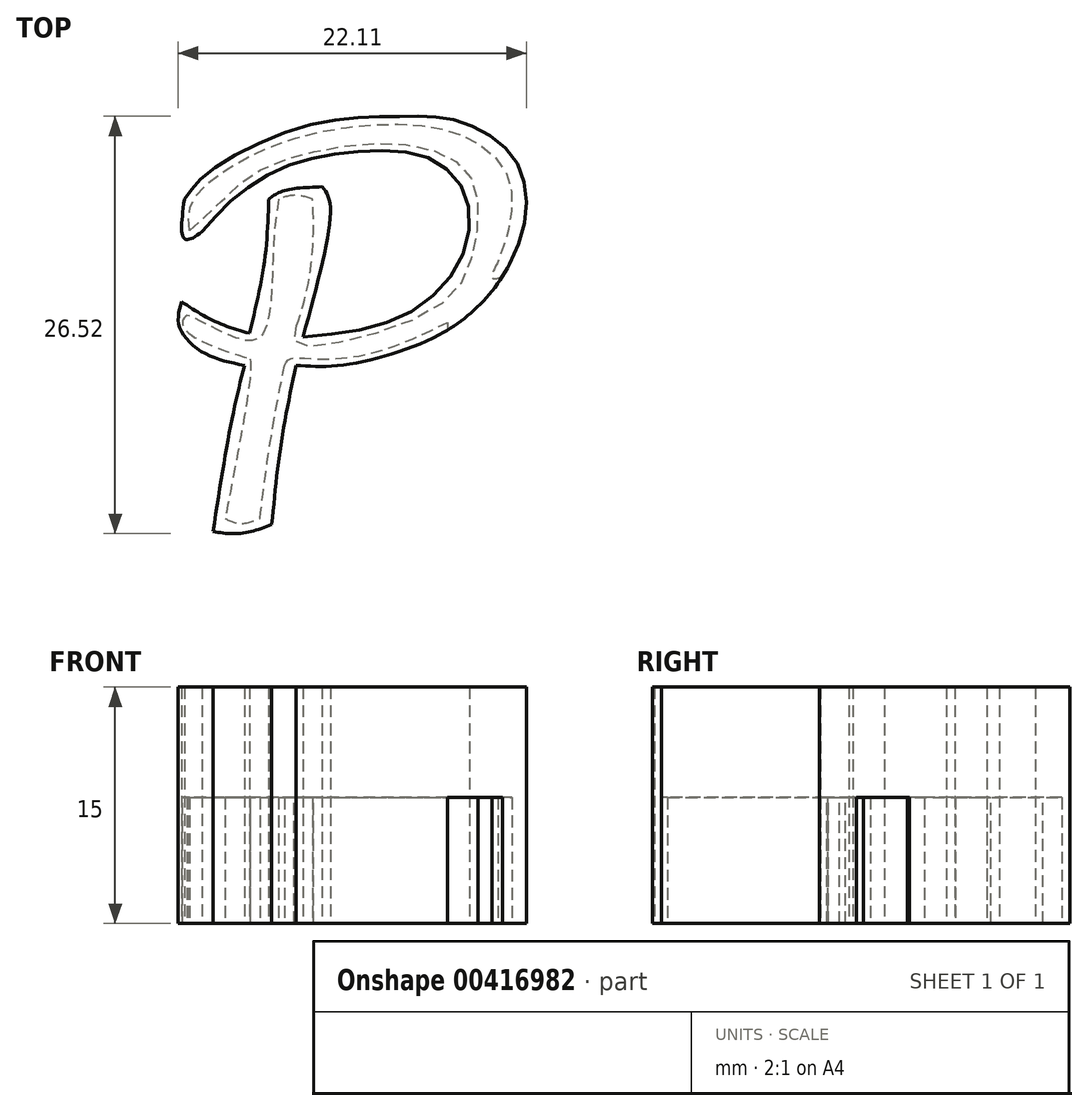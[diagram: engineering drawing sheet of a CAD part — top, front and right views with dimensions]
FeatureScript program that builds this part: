
annotation { "Feature Type Name" : "Feature", "Feature Type Description" : "" }
export const myFeature = defineFeature(function(context is Context, id is Id, definition is map)
    precondition{}
    {
        {
            var Q0;
            Q0=qCreatedBy(makeId("Top.planeOp"),FACE);
            var sketch = newSketch(context, id + "F0", { "sketchPlane" : qUnion([Q0])});
            skFitSpline(sketch, "E0", {"points": [v(-29.52, 16.09) * mm, v(-21.73, 24.17) * mm, v(-15.95, 22) * mm], "startDerivative": vector(5.63, 25.07) * mm, "endDerivative": vector(12.64, -16.05) * mm});
            skFitSpline(sketch, "E1", {"points": [v(-29.52, 16.09) * mm, v(-29.52, 11.79) * mm, v(-26.49, 8.08) * mm, v(-18.6, 8.9) * mm, v(-11.86, 14.14) * mm], "startDerivative": vector(-2.65, -20.74) * mm, "endDerivative": vector(20.85, 20.56) * mm});
            skFitSpline(sketch, "E2", {"points": [v(-15.95, 22) * mm, v(-15.95, 19.53) * mm, v(-19.6, 15.68) * mm, v(-26.31, 14.5) * mm], "startDerivative": vector(1.91, -9.63) * mm, "endDerivative": vector(-17.6, -0.63) * mm});
            skFitSpline(sketch, "E3", {"points": [v(-26.31, 14.5) * mm, v(-26.31, 12.31) * mm, v(-24.25, 10.14) * mm, v(-18.22, 11.13) * mm, v(-11.16, 17.2) * mm], "startDerivative": vector(-1.95, -12.78) * mm, "endDerivative": vector(19.15, 20.18) * mm});
            skFitSpline(sketch, "E4", {"points": [v(-11.16, 17.2) * mm, v(-8.94, 21.18) * mm, v(-5, 24.17) * mm, v(-0.8, 24.22) * mm, v(2.15, 22.9) * mm], "startDerivative": vector(7.17, 15.76) * mm, "endDerivative": vector(12.55, -6.92) * mm});
            skFitSpline(sketch, "E5", {"points": [v(2.15, 22.9) * mm, v(2.96, 23.95) * mm, v(5.9, 24.4) * mm], "startDerivative": vector(1.46, 2.97) * mm, "endDerivative": vector(5.76, 0.2) * mm});
            skFitSpline(sketch, "E6", {"points": [v(-11.86, 14.14) * mm, v(-11.86, 10.9) * mm, v(-9.94, 8.05) * mm, v(-6.14, 8.37) * mm], "startDerivative": vector(-1.2, -9.86) * mm, "endDerivative": vector(11.9, 3.41) * mm});
            skFitSpline(sketch, "E7", {"points": [v(-6.14, 8.37) * mm, v(-2.1, 12.17) * mm, v(0.93, 17.2) * mm], "startDerivative": vector(8.72, 7.18) * mm, "endDerivative": vector(5.42, 10.46) * mm});
            skFitSpline(sketch, "E8", {"points": [v(0.93, 17.2) * mm, v(0.93, 11.63) * mm, v(3.05, 8.96) * mm, v(6.72, 9.41) * mm, v(12.48, 14.14) * mm], "startDerivative": vector(-2.53, -22.33) * mm, "endDerivative": vector(18.4, 18.48) * mm});
            skFitSpline(sketch, "E9", {"points": [v(5.9, 24.4) * mm, v(4.28, 19.57) * mm, v(4.12, 12.84) * mm, v(5.03, 11.7) * mm, v(7.94, 12.57) * mm, v(12.9, 17.2) * mm], "startDerivative": vector(-8.65, -19.72) * mm, "endDerivative": vector(19.75, 21.62) * mm});
            skFitSpline(sketch, "E10", {"points": [v(12.9, 17.2) * mm, v(14.78, 20.91) * mm, v(18.92, 23.71) * mm, v(21.5, 24.4) * mm, v(24.04, 24.4) * mm, v(25.8, 23.42) * mm, v(26.53, 22.62) * mm, v(26.53, 21.34) * mm], "startDerivative": vector(7.3, 21.14) * mm, "endDerivative": vector(-1.85, -13.72) * mm});
            skFitSpline(sketch, "E11", {"points": [v(26.53, 21.34) * mm, v(25.28, 20.25) * mm, v(23.65, 19.61) * mm], "startDerivative": vector(-2.36, -2.44) * mm, "endDerivative": vector(-3.4, -1.02) * mm});
            skFitSpline(sketch, "E12", {"points": [v(23.65, 19.61) * mm, v(23.65, 21.34) * mm, v(22.59, 22.59) * mm, v(19.84, 22.59) * mm, v(16.5, 19.47) * mm, v(15.44, 17.2) * mm, v(15.32, 13.21) * mm, v(17.37, 9.82) * mm, v(20.92, 9.28) * mm, v(26.53, 12.94) * mm, v(29.59, 16.3) * mm], "startDerivative": vector(3.16, 25.43) * mm, "endDerivative": vector(23.14, 28.11) * mm});
            skFitSpline(sketch, "E13", {"points": [v(12.48, 14.14) * mm, v(12.48, 11.74) * mm, v(14.3, 8.6) * mm, v(16.78, 7.12) * mm, v(20.7, 7.08) * mm, v(24.82, 9.2) * mm, v(29.53, 13.7) * mm], "startDerivative": vector(-2.82, -18.44) * mm, "endDerivative": vector(21.23, 22.93) * mm});
            skFitSpline(sketch, "E14", {"points": [v(29.59, 16.3) * mm, v(30.44, 19.1) * mm, v(33.77, 22.87) * mm, v(38.3, 24.54) * mm, v(41.2, 24.05) * mm, v(42.85, 22.55) * mm, v(43.33, 20.19) * mm, v(41.47, 17.24) * mm, v(36.7, 14.68) * mm, v(32.8, 14.36) * mm], "startDerivative": vector(5.2, 27.04) * mm, "endDerivative": vector(-32.45, 0.66) * mm});
            skFitSpline(sketch, "E15", {"points": [v(32.8, 14.36) * mm, v(32.8, 12.43) * mm, v(34.32, 10.34) * mm, v(38.4, 10.26) * mm, v(45.36, 14.68) * mm, v(50.16, 20.77) * mm], "startDerivative": vector(-1.91, -14.46) * mm, "endDerivative": vector(16.23, 24.12) * mm});
            skFitSpline(sketch, "E16", {"points": [v(29.53, 13.7) * mm, v(29.53, 12.01) * mm, v(31.32, 8.9) * mm, v(35.92, 7.67) * mm, v(42.01, 9.84) * mm, v(46.54, 13.35) * mm, v(49.86, 17.2) * mm, v(51.72, 20.2) * mm], "startDerivative": vector(-2.56, -18.37) * mm, "endDerivative": vector(12.98, 22.51) * mm});
            skLineSegment(sketch, "E17", {"start": v(50.16, 20.77) * mm, "end": v(51.72, 20.2) * mm});
            skFitSpline(sketch, "E18", {"points": [v(-26.18, 16.08) * mm, v(-25.34, 19.37) * mm, v(-22.06, 22.5) * mm, v(-19.63, 22.7) * mm, v(-18.72, 21.74) * mm, v(-18.99, 19.53) * mm, v(-20.98, 17.43) * mm, v(-24.32, 16.09) * mm, v(-26.18, 16.08) * mm]});
            skFitSpline(sketch, "E19", {"points": [v(-8.92, 15.05) * mm, v(-8.16, 18.38) * mm, v(-5.66, 21.9) * mm, v(-2.78, 22.4) * mm, v(1.45, 20.49) * mm], "startDerivative": vector(1.92, 13.6) * mm, "endDerivative": vector(15.76, -8.92) * mm});
            skFitSpline(sketch, "E20", {"points": [v(-8.92, 15.05) * mm, v(-8.92, 12.3) * mm, v(-7.52, 10.82) * mm, v(-5.4, 11.59) * mm, v(-1.43, 16.26) * mm, v(1.45, 20.49) * mm], "startDerivative": vector(-2.38, -16.28) * mm, "endDerivative": vector(10.96, 16.58) * mm});
            skFitSpline(sketch, "E21", {"points": [v(32.96, 15.95) * mm, v(33.77, 19.4) * mm, v(37.64, 22.68) * mm, v(40.06, 22.25) * mm, v(40.28, 19.67) * mm, v(36.73, 16.81) * mm, v(32.96, 15.95) * mm]});
            skLineSegment(sketch, "E22", {"start": v(-26.49, 8.08) * mm, "end": v(-26.49, 0) * mm});
            skFitSpline(sketch, "E23", {"points": [v(-39.17, 6.72) * mm, v(-38.6, 11.78) * mm, v(-37.63, 16.84) * mm], "startDerivative": vector(0.97, 10.16) * mm, "endDerivative": vector(2.1, 10.07) * mm});
            skFitSpline(sketch, "E24", {"points": [v(-37.63, 16.84) * mm, v(-34.88, 16.84) * mm, v(-29.82, 18.18) * mm, v(-25.73, 20.94) * mm, v(-23.16, 25.68) * mm, v(-23.8, 30.03) * mm, v(-27.45, 32.4) * mm, v(-31.17, 32.65) * mm, v(-36.87, 32.08) * mm, v(-43.4, 28.94) * mm, v(-44.72, 27.4) * mm], "startDerivative": vector(32.12, -2.24) * mm, "endDerivative": vector(-16.47, -20.53) * mm});
            skFitSpline(sketch, "E25", {"points": [v(-44.72, 27.4) * mm, v(-44.72, 24.9) * mm, v(-43.59, 25.35) * mm], "startDerivative": vector(-0.9, -6.83) * mm, "endDerivative": vector(3.83, 3.23) * mm});
            skFitSpline(sketch, "E26", {"points": [v(-43.59, 25.35) * mm, v(-41.22, 27.74) * mm, v(-37.57, 29.72) * mm, v(-33.41, 30.43) * mm, v(-29.25, 30.04) * mm, v(-26.82, 27.48) * mm, v(-27.33, 23.26) * mm, v(-31.24, 19.8) * mm, v(-37.2, 18.65) * mm], "startDerivative": vector(19.6, 22.42) * mm, "endDerivative": vector(-42.14, -3.8) * mm});
            skFitSpline(sketch, "E27", {"points": [v(-37.2, 18.65) * mm, v(-35.46, 27.03) * mm, v(-35.97, 28.19) * mm], "startDerivative": vector(3.92, 14.3) * mm, "endDerivative": vector(-2.43, 3.12) * mm});
            skFitSpline(sketch, "E28", {"points": [v(-35.97, 28.19) * mm, v(-38.52, 27.9) * mm, v(-39.36, 27.39) * mm], "startDerivative": vector(-4.73, -0.2) * mm, "endDerivative": vector(-1.82, -1.5) * mm});
            skFitSpline(sketch, "E29", {"points": [v(-39.17, 6.72) * mm, v(-41.13, 6.17) * mm, v(-42.9, 6.28) * mm], "startDerivative": vector(-3.82, -1.4) * mm, "endDerivative": vector(-3.65, 0.53) * mm});
            skFitSpline(sketch, "E30", {"points": [v(-42.9, 6.28) * mm, v(-41.77, 13.06) * mm, v(-40.91, 16.84) * mm], "startDerivative": vector(1.97, 12.75) * mm, "endDerivative": vector(2.02, 8.15) * mm});
            skFitSpline(sketch, "E31", {"points": [v(-40.91, 16.84) * mm, v(-43.59, 17.7) * mm, v(-45.06, 19.36) * mm, v(-44.9, 20.89) * mm], "startDerivative": vector(-7.42, 1.53) * mm, "endDerivative": vector(1.61, 5.39) * mm});
            skFitSpline(sketch, "E32", {"points": [v(-44.9, 20.89) * mm, v(-42.9, 19.69) * mm, v(-40.59, 18.88) * mm], "startDerivative": vector(3.9, -2.64) * mm, "endDerivative": vector(4.7, -1.38) * mm});
            skFitSpline(sketch, "E33", {"points": [v(-40.59, 18.88) * mm, v(-39.64, 23.42) * mm, v(-39.36, 27.39) * mm], "startDerivative": vector(2.16, 8.87) * mm, "endDerivative": vector(0.27, 8.13) * mm});
            skSolve(sketch);
        }
        {
            var Q0;
            {var subQ1=sQuery(id+"F0.wireOp",EDGE,"E23");Q0=makeQuery(id+"F0.imprint","IMPRINT",FACE,{"disambiguationData":[TD([[makeQuery(id+"F0.imprint","IMPRINT",EDGE,{"derivedFrom":subQ1}),1.0]])]});}
            var Q1;
            {var subQ3=sQuery(id+"F0.wireOp",EDGE,"E0");Q1=makeQuery(id+"F0.imprint","IMPRINT",FACE,{"disambiguationData":[TD([[makeQuery(id+"F0.imprint","IMPRINT",EDGE,{"derivedFrom":subQ3}),-1.0]])]});}
            extrude(context, id + "F1", {"entities" : qUnion([Q0, Q1]), "depth" : 15 * mm});
        }
        {
            var Q0;
            {var subQ0=sQuery(id+"F0.wireOp",EDGE,"E0");var subQ2=sQuery(id+"F0.wireOp",EDGE,"E33");var subQ6=sQuery(id+"F0.wireOp",EDGE,"E32");var subQ8=sQuery(id+"F0.wireOp",EDGE,"E31");var subQ9=sQuery(id+"F0.wireOp",EDGE,"E30");var subQ12=sQuery(id+"F0.wireOp",EDGE,"E29");var subQ13=sQuery(id+"F0.wireOp",EDGE,"E28");var subQ14=sQuery(id+"F0.wireOp",EDGE,"E27");var subQ15=sQuery(id+"F0.wireOp",EDGE,"E26");var subQ16=sQuery(id+"F0.wireOp",EDGE,"E25");var subQ17=sQuery(id+"F0.wireOp",EDGE,"E24");var subQ18=sQuery(id+"F0.wireOp",EDGE,"E0");var subQ19=sQuery(id+"F0.wireOp",EDGE,"E23");var subQ20=sQuery(id+"F0.wireOp",EDGE,"E8");var subQ21=sQuery(id+"F0.wireOp",EDGE,"E7");var subQ22=sQuery(id+"F0.wireOp",EDGE,"E6");var subQ23=sQuery(id+"F0.wireOp",EDGE,"E5");var subQ24=sQuery(id+"F0.wireOp",EDGE,"E4");var subQ25=sQuery(id+"F0.wireOp",EDGE,"E9");var subQ26=sQuery(id+"F0.wireOp",EDGE,"E21");var subQ27=sQuery(id+"F0.wireOp",EDGE,"E3");var subQ28=sQuery(id+"F0.wireOp",EDGE,"E1");var subQ29=sQuery(id+"F0.wireOp",EDGE,"E2");var subQ30=sQuery(id+"F0.wireOp",EDGE,"E10");var subQ31=sQuery(id+"F0.wireOp",EDGE,"E11");var subQ32=sQuery(id+"F0.wireOp",EDGE,"E12");var subQ33=sQuery(id+"F0.wireOp",EDGE,"E13");var subQ34=sQuery(id+"F0.wireOp",EDGE,"E14");var subQ35=sQuery(id+"F0.wireOp",EDGE,"E15");var subQ36=sQuery(id+"F0.wireOp",EDGE,"E16");var subQ37=sQuery(id+"F0.wireOp",EDGE,"E17");var subQ38=sQuery(id+"F0.wireOp",EDGE,"E19");var subQ39=sQuery(id+"F0.wireOp",EDGE,"E20");Q0=makeQuery(id+"FnfwpsjC2COg8uT_1.boolean.opBoolean","SPLIT",FACE,{"disambiguationData":[TD([makeQuery(id+"F1.opExtrude","SWEPT_FACE",FACE,{"disambiguationData":[OSD([subQ18])]})])],"derivedFrom":makeQuery(id+"F1.opExtrude","CAP_FACE",FACE,{"disambiguationData":[OSD([subQ18,subQ28,subQ29,subQ27,subQ24,subQ23,subQ22,subQ21,subQ20,subQ25,subQ30,subQ31,subQ32,subQ33,subQ34,subQ35,subQ36,subQ37,sQuery(id+"F0.wireOp",EDGE,"E18"),subQ38,subQ39,subQ26,subQ19,subQ17,subQ16,subQ15,subQ14,subQ13,subQ12,subQ9,subQ8,subQ6,subQ2,subQ0])],"isStart":true})});}
            var sketch = newSketch(context, id + "F2", { "sketchPlane" : qUnion([Q0])});
            skFitSpline(sketch, "E34", {"points": [v(-7.05, -22.42) * mm, v(-4.76, -23.59) * mm, v(-1.87, -23.71) * mm, v(2.2, -22.24) * mm], "startDerivative": vector(7.38, -4.6) * mm, "endDerivative": vector(10.81, 4.77) * mm});
            skFitSpline(sketch, "E35", {"points": [v(2.2, -22.24) * mm, v(3.4, -23.59) * mm, v(4.89, -23.59) * mm, v(4.9, -23.59) * mm], "startDerivative": vector(1.78, -3.5) * mm, "endDerivative": vector(0.19, -0.04) * mm});
            skFitSpline(sketch, "E36", {"points": [v(4.9, -23.59) * mm, v(3.69, -19.61) * mm, v(3.13, -14.5) * mm, v(3.88, -11) * mm, v(7.5, -11.57) * mm, v(12.9, -16.09) * mm], "startDerivative": vector(-7.2, 20.2) * mm, "endDerivative": vector(21.14, -21.2) * mm});
            skFitSpline(sketch, "E37", {"points": [v(-6.01, -9.18) * mm, v(-3.7, -11.12) * mm, v(-1.23, -14.14) * mm, v(0.87, -18.02) * mm], "startDerivative": vector(7.8, -6) * mm, "endDerivative": vector(5.45, -11.06) * mm});
            skFitSpline(sketch, "E38", {"points": [v(0.87, -18.02) * mm, v(1.57, -18.02) * mm, v(1.16, -14.78) * mm, v(2.12, -10.74) * mm, v(4.69, -9.55) * mm, v(8, -10.74) * mm, v(13.04, -15.04) * mm], "startDerivative": vector(11.28, -3.14) * mm, "endDerivative": vector(21.76, -20.55) * mm});
            skFitSpline(sketch, "E39", {"points": [v(16.32, -9.88) * mm, v(18.15, -8.49) * mm, v(21.8, -8.93) * mm, v(29.59, -15.35) * mm], "startDerivative": vector(7.05, 7.31) * mm, "endDerivative": vector(16.95, -16.56) * mm});
            skFitSpline(sketch, "E40", {"points": [v(13.04, -15.04) * mm, v(13.04, -12.56) * mm, v(14.6, -9.02) * mm, v(17.92, -7.33) * mm, v(22.52, -8.37) * mm, v(29.53, -14.14) * mm], "startDerivative": vector(-1.45, 15.7) * mm, "endDerivative": vector(25.27, -24.15) * mm});
            skFitSpline(sketch, "E41", {"points": [v(12.9, -16.09) * mm, v(14.9, -20.41) * mm, v(19.74, -23.72) * mm, v(24.12, -23.98) * mm, v(25.9, -21.89) * mm], "startDerivative": vector(5.56, -17.35) * mm, "endDerivative": vector(7.1, 12.74) * mm});
            skFitSpline(sketch, "E42", {"points": [v(29.59, -15.35) * mm, v(31.16, -19.52) * mm, v(35.37, -23.38) * mm, v(39.89, -24.04) * mm, v(41.96, -22.95) * mm], "startDerivative": vector(4.34, -16.27) * mm, "endDerivative": vector(9.61, 7.15) * mm});
            skFitSpline(sketch, "E43", {"points": [v(41.96, -22.95) * mm, v(42.83, -20.46) * mm, v(40.82, -17.49) * mm, v(36.23, -15.16) * mm, v(32.5, -14.85) * mm], "startDerivative": vector(6.75, 11.6) * mm, "endDerivative": vector(-14.39, -0.1) * mm});
            skFitSpline(sketch, "E44", {"points": [v(32.5, -14.85) * mm, v(32.08, -12.6) * mm, v(33.51, -9.88) * mm, v(37.87, -9.35) * mm, v(43.64, -12.54) * mm, v(48.24, -17.3) * mm, v(50.27, -20.1) * mm], "startDerivative": vector(-5.9, 17.41) * mm, "endDerivative": vector(11.9, -17.42) * mm});
            skFitSpline(sketch, "E45", {"points": [v(29.53, -14.14) * mm, v(30.02, -14.14) * mm, v(30.05, -13.7) * mm], "startDerivative": vector(1.2, -0.23) * mm, "endDerivative": vector(-0.16, 1.13) * mm});
            skFitSpline(sketch, "E46", {"points": [v(30.05, -13.7) * mm, v(30.05, -12.45) * mm, v(30.92, -10.3) * mm, v(32.8, -8.62) * mm, v(37.33, -8.23) * mm, v(44.03, -11.82) * mm, v(50.87, -19.69) * mm], "startDerivative": vector(-1.32, 12.84) * mm, "endDerivative": vector(24.94, -32.81) * mm});
            skFitSpline(sketch, "E47", {"points": [v(50.87, -19.69) * mm, v(50.72, -20.07) * mm, v(50.27, -20.1) * mm], "startDerivative": vector(-0.16, -0.96) * mm, "endDerivative": vector(-1.02, 0.13) * mm});
            skFitSpline(sketch, "E48", {"points": [v(-6.01, -9.18) * mm, v(-8.26, -8.43) * mm, v(-9.9, -8.8) * mm, v(-11.25, -11.3) * mm, v(-11.22, -14.93) * mm, v(-10.36, -18.1) * mm, v(-7.05, -22.42) * mm], "startDerivative": vector(-15.85, 6.69) * mm, "endDerivative": vector(17.73, -20.1) * mm});
            skFitSpline(sketch, "E49", {"points": [v(-44.4, -25.41) * mm, v(-44.42, -26.6) * mm, v(-43.82, -27.83) * mm, v(-40.33, -30.25) * mm, v(-35.04, -31.87) * mm, v(-29.66, -32.07) * mm, v(-26.22, -31.02) * mm, v(-24.15, -28.75) * mm, v(-24.07, -25.76) * mm, v(-24.8, -23.44) * mm], "startDerivative": vector(-1.7, -17.79) * mm, "endDerivative": vector(-8.36, 22.42) * mm});
            skFitSpline(sketch, "E50", {"points": [v(-44.4, -25.41) * mm, v(-42.67, -26.98) * mm, v(-40.35, -29) * mm, v(-36.56, -30.4) * mm, v(-31.68, -30.95) * mm, v(-27.89, -30.05) * mm, v(-26.24, -28.08) * mm, v(-26.4, -24.04) * mm, v(-28.2, -20.89) * mm, v(-34.51, -18.38) * mm, v(-37.65, -18.27) * mm, v(-37.58, -19.36) * mm], "startDerivative": vector(22.63, -19.9) * mm, "endDerivative": vector(7.92, -25.16) * mm});
            skFitSpline(sketch, "E51", {"points": [v(-37.58, -19.36) * mm, v(-36.88, -21.94) * mm, v(-36.52, -25.35) * mm, v(-36.6, -27.4) * mm], "startDerivative": vector(2.34, -7.27) * mm, "endDerivative": vector(-0.45, -6.48) * mm});
            skFitSpline(sketch, "E52", {"points": [v(-36.6, -27.4) * mm, v(-37.7, -27.64) * mm, v(-38.74, -27.4) * mm], "startDerivative": vector(-2.2, -0.72) * mm, "endDerivative": vector(-2.1, 0.72) * mm});
            skFitSpline(sketch, "E53", {"points": [v(-38.74, -27.4) * mm, v(-39.07, -24.24) * mm, v(-39.74, -18.83) * mm, v(-41.3, -18.53) * mm, v(-44.06, -19.83) * mm, v(-44.56, -20) * mm], "startDerivative": vector(-1.77, 11.76) * mm, "endDerivative": vector(-4.2, -0.93) * mm});
            skFitSpline(sketch, "E54", {"points": [v(-44.56, -20) * mm, v(-44.84, -19.65) * mm, v(-44.43, -18.88) * mm, v(-40.55, -17.26) * mm], "startDerivative": vector(-2, 1.67) * mm, "endDerivative": vector(8.5, 2.72) * mm});
            skFitSpline(sketch, "E55", {"points": [v(-40.55, -17.26) * mm, v(-40.55, -16.14) * mm, v(-41.36, -11.13) * mm, v(-42.14, -7.11) * mm], "startDerivative": vector(0.33, 4.49) * mm, "endDerivative": vector(-1.9, 9.72) * mm});
            skFitSpline(sketch, "E56", {"points": [v(-42.14, -7.11) * mm, v(-41.19, -6.8) * mm, v(-39.92, -7.11) * mm], "startDerivative": vector(1.96, 0.98) * mm, "endDerivative": vector(2.47, -0.94) * mm});
            skFitSpline(sketch, "E57", {"points": [v(-39.92, -7.11) * mm, v(-39.35, -11.42) * mm, v(-38.37, -16.84) * mm], "startDerivative": vector(1.04, -8.9) * mm, "endDerivative": vector(2.04, -10.52) * mm});
            skFitSpline(sketch, "E58", {"points": [v(-38.37, -16.84) * mm, v(-38, -17.26) * mm, v(-36.6, -17.26) * mm, v(-32.74, -17.64) * mm, v(-28.02, -19.56) * mm], "startDerivative": vector(2.36, -4.17) * mm, "endDerivative": vector(12.76, -6.2) * mm});
            skFitSpline(sketch, "E59", {"points": [v(-28.02, -19.56) * mm, v(-28.02, -18.8) * mm, v(-28.53, -16.84) * mm, v(-29.12, -13.32) * mm, v(-27.52, -9.7) * mm, v(-24.8, -8.3) * mm, v(-21.71, -8.4) * mm], "startDerivative": vector(0.62, 7.7) * mm, "endDerivative": vector(17.21, -2.04) * mm});
            skFitSpline(sketch, "E60", {"points": [v(-21.71, -8.4) * mm, v(-19.26, -9.1) * mm, v(-15.42, -11.56) * mm, v(-11.22, -14.93) * mm], "startDerivative": vector(8.93, -1.76) * mm, "endDerivative": vector(10.85, -8.94) * mm});
            skFitSpline(sketch, "E61", {"points": [v(-24.8, -23.44) * mm, v(-25.15, -22.39) * mm, v(-24.02, -22.7) * mm], "startDerivative": vector(-1.45, 2.82) * mm, "endDerivative": vector(2.97, -1.33) * mm});
            skFitSpline(sketch, "E62", {"points": [v(-24.02, -22.7) * mm, v(-22.57, -23.46) * mm, v(-20.73, -24) * mm, v(-18.78, -23.7) * mm, v(-17.26, -22.7) * mm, v(-16.36, -21.26) * mm, v(-16.76, -19.12) * mm, v(-18.63, -16.98) * mm, v(-22.45, -15.23) * mm, v(-26.71, -15) * mm], "startDerivative": vector(15.3, -8.48) * mm, "endDerivative": vector(-29, -0.92) * mm});
            skFitSpline(sketch, "E63", {"points": [v(-26.71, -15) * mm, v(-27, -13.4) * mm, v(-26.71, -10.83) * mm, v(-24.53, -9.53) * mm, v(-21.82, -9.39) * mm, v(-17.7, -10.97) * mm, v(-10.85, -16.84) * mm], "startDerivative": vector(-2.82, 12.71) * mm, "endDerivative": vector(26.37, -25.43) * mm});
            skPoint(sketch, "E64.0.internal.orphan", {"position": v(-9.68, -15.93) * mm});
            skPoint(sketch, "E64.1.internal.orphan", {"position": v(-9.68, -13.28) * mm});
            skPoint(sketch, "E64.endDerivative.orphan", {"position": v(-5.56, -10.74) * mm});
            skPoint(sketch, "E65.endDerivative.orphan", {"position": v(1.16, -19.18) * mm});
            skPoint(sketch, "E66.2.internal.orphan", {"position": v(23.92, -21.89) * mm});
            skPoint(sketch, "E67.0.internal.orphan", {"position": v(22.52, -23.1) * mm});
            skPoint(sketch, "E67.1.internal.orphan", {"position": v(20.68, -23.1) * mm});
            skFitSpline(sketch, "E68", {"points": [v(16.32, -9.88) * mm, v(14.74, -12.36) * mm, v(14.9, -17.64) * mm, v(17.49, -21.57) * mm, v(20.07, -23.1) * mm], "startDerivative": vector(-8.57, -9.78) * mm, "endDerivative": vector(11.94, -5.63) * mm});
            skFitSpline(sketch, "E69", {"points": [v(20.07, -23.1) * mm, v(21.65, -23.39) * mm, v(23.65, -22.64) * mm, v(24.37, -20.44) * mm], "startDerivative": vector(4.94, -1.48) * mm, "endDerivative": vector(0.96, 7.02) * mm});
            skFitSpline(sketch, "E70", {"points": [v(24.37, -20.44) * mm, v(25.55, -20.86) * mm, v(25.9, -21.89) * mm], "startDerivative": vector(2.68, -0.47) * mm, "endDerivative": vector(0.36, -2.46) * mm});
            skSolve(sketch);
        }
        {
            var Q0;
            Q0 = qSketchRegion(id + "F2", true);
            extrude(context, id + "F3", {"entities" : qUnion([Q0]), "operationType" : NewBodyOperationType.REMOVE, "oppositeDirection" : true, "depth" : 8 * mm});
        }
    });
